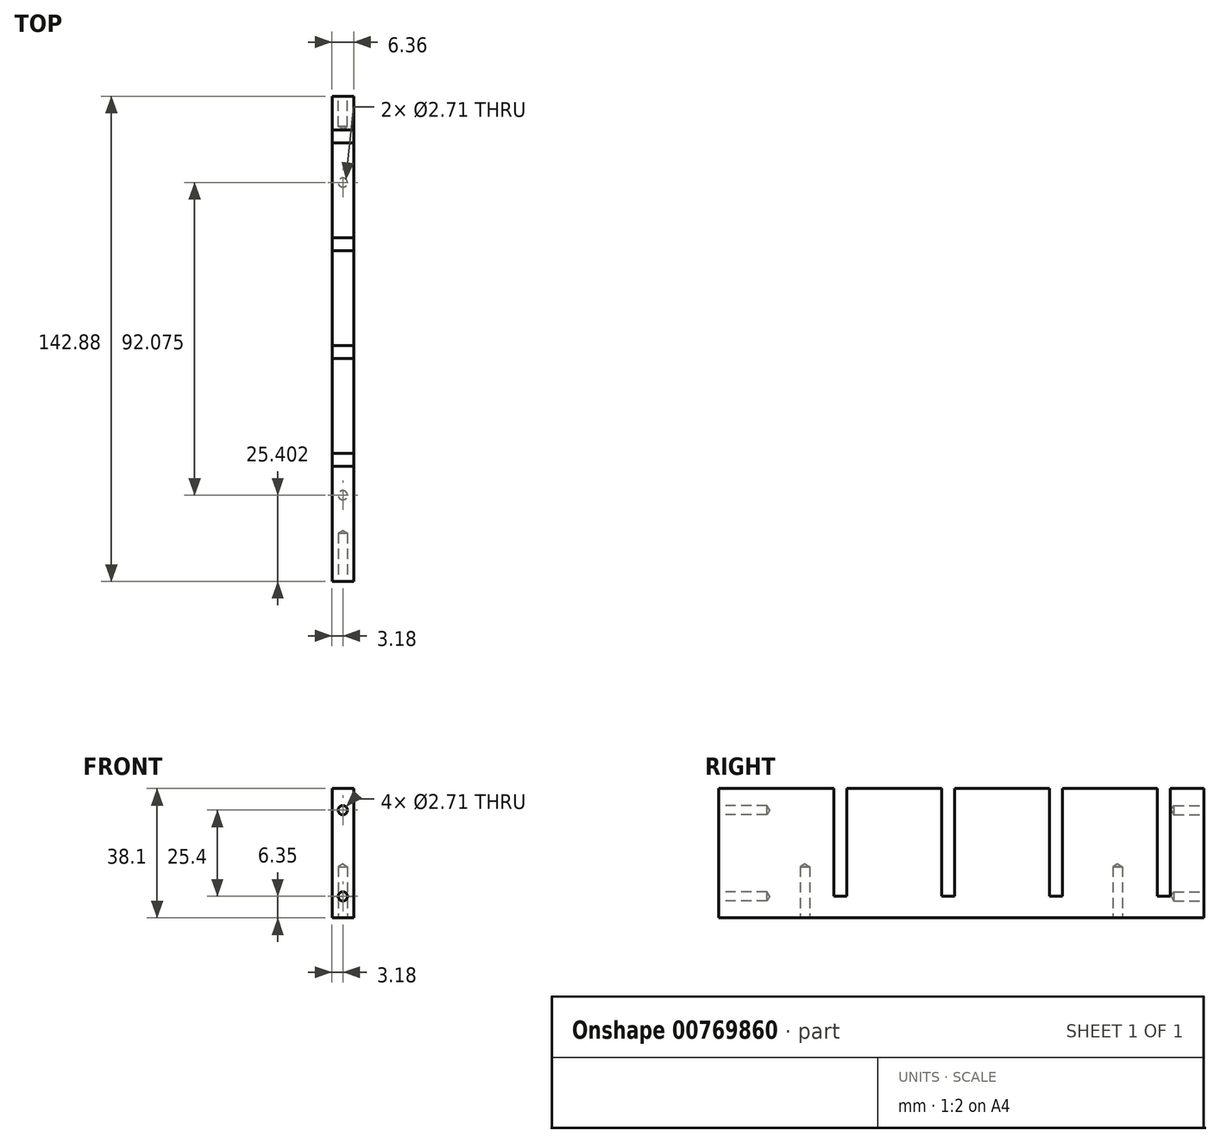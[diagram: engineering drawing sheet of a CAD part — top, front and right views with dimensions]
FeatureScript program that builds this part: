
annotation { "Feature Type Name" : "Feature", "Feature Type Description" : "" }
export const myFeature = defineFeature(function(context is Context, id is Id, definition is map)
    precondition{}
    {
        {
            var Q0;
            Q0=qCreatedBy(makeId("Top.planeOp"),FACE);
            var sketch = newSketch(context, id + "F0", { "sketchPlane" : qUnion([Q0])});
            skLineSegment(sketch, "E0.bottom", {"start": v(-3.17, 71.44) * mm, "end": v(3.18, 71.44) * mm});
            skLineSegment(sketch, "E0.top", {"start": v(-3.18, -71.44) * mm, "end": v(3.17, -71.44) * mm});
            skLineSegment(sketch, "E0.left", {"start": v(-3.17, 71.44) * mm, "end": v(-3.18, -71.44) * mm});
            skLineSegment(sketch, "E0.right", {"start": v(3.18, 71.44) * mm, "end": v(3.17, -71.44) * mm});
            skLineSegment(sketch, "E1", {"start": v(3.18, 71.44) * mm, "end": v(-3.18, -71.44) * mm, "construction": true});
            skSolve(sketch);
        }
        {
            var Q0;
            Q0=qSketchRegion(id+"F0",true);
            extrude(context, id + "F1", {"entities" : qUnion([Q0]), "depth" : 38.1 * mm, "offsetDistance" : 25.4 * mm});
        }
        {
            var Q0;
            Q0=makeQuery(id+"F1.opExtrude","SWEPT_FACE",FACE,{"disambiguationData":[OSD([sQuery(id+"F0.wireOp",EDGE,"E0.right")])]});
            var sketch = newSketch(context, id + "F2", { "sketchPlane" : qUnion([Q0])});
            skLineSegment(sketch, "E2", {"start": v(-71.44, 6.35) * mm, "end": v(71.44, 6.35) * mm, "construction": true});
            skLineSegment(sketch, "E3.bottom", {"start": v(61.53, 38.1) * mm, "end": v(57.72, 38.1) * mm});
            skLineSegment(sketch, "E3.top", {"start": v(61.53, 6.35) * mm, "end": v(57.72, 6.35) * mm});
            skLineSegment(sketch, "E3.left", {"start": v(61.53, 38.1) * mm, "end": v(61.53, 6.35) * mm});
            skLineSegment(sketch, "E3.right", {"start": v(57.72, 38.1) * mm, "end": v(57.72, 6.35) * mm});
            skLineSegment(sketch, "E4.bottom", {"start": v(29.78, 38.1) * mm, "end": v(25.97, 38.1) * mm});
            skLineSegment(sketch, "E4.top", {"start": v(29.78, 6.35) * mm, "end": v(25.97, 6.35) * mm});
            skLineSegment(sketch, "E4.left", {"start": v(29.78, 38.1) * mm, "end": v(29.78, 6.35) * mm});
            skLineSegment(sketch, "E4.right", {"start": v(25.97, 38.1) * mm, "end": v(25.97, 6.35) * mm});
            skLineSegment(sketch, "E5.bottom", {"start": v(-1.97, 38.1) * mm, "end": v(-5.78, 38.1) * mm});
            skLineSegment(sketch, "E5.top", {"start": v(-1.97, 6.35) * mm, "end": v(-5.78, 6.35) * mm});
            skLineSegment(sketch, "E5.left", {"start": v(-1.97, 38.1) * mm, "end": v(-1.97, 6.35) * mm});
            skLineSegment(sketch, "E5.right", {"start": v(-5.78, 38.1) * mm, "end": v(-5.78, 6.35) * mm});
            skLineSegment(sketch, "E6.bottom", {"start": v(-33.72, 38.1) * mm, "end": v(-37.53, 38.1) * mm});
            skLineSegment(sketch, "E6.top", {"start": v(-33.72, 6.35) * mm, "end": v(-37.53, 6.35) * mm});
            skLineSegment(sketch, "E6.left", {"start": v(-33.72, 38.1) * mm, "end": v(-33.72, 6.35) * mm});
            skLineSegment(sketch, "E6.right", {"start": v(-37.53, 38.1) * mm, "end": v(-37.53, 6.35) * mm});
            skPoint(sketch, "E7", {"position": v(59.62, 6.35) * mm});
            skPoint(sketch, "E8", {"position": v(27.87, 6.35) * mm});
            skPoint(sketch, "E9", {"position": v(-3.88, 6.35) * mm});
            skPoint(sketch, "E10", {"position": v(-35.63, 6.35) * mm});
            skSolve(sketch);
        }
        {
            var Q0;
            Q0 = qSketchRegion(id + "F2", true);
            extrude(context, id + "F3", {"entities" : qUnion([Q0]), "operationType" : NewBodyOperationType.REMOVE, "endBound" : BoundingType.THROUGH_ALL, "oppositeDirection" : true, "depth" : 25.4 * mm, "offsetDistance" : 25.4 * mm});
        }
        {
            var Q0;
            Q0=makeQuery(id+"F1.opExtrude","CAP_FACE",FACE,{"disambiguationData":[OSD([sQuery(id+"F0.wireOp",EDGE,"E0.bottom"),sQuery(id+"F0.wireOp",EDGE,"E0.top"),sQuery(id+"F0.wireOp",EDGE,"E0.left"),sQuery(id+"F0.wireOp",EDGE,"E0.right")])],"isStart":true});
            var sketch = newSketch(context, id + "F4", { "sketchPlane" : qUnion([Q0])});
            skLineSegment(sketch, "E11", {"start": v(0, 71.44) * mm, "end": v(0, -71.44) * mm, "construction": true});
            skPoint(sketch, "E12", {"position": v(0, 46.04) * mm});
            skPoint(sketch, "E13", {"position": v(0, -46.04) * mm});
            skSolve(sketch);
        }
        {
            var Q0;
            Q0=sQuery(id+"F4.wireOp",VERTEX,"E12");
            var Q1;
            Q1=sQuery(id+"F4.wireOp",VERTEX,"E13");
            var Q2;
            Q2=makeQuery(id+"F1.opExtrude","SWEPT_BODY",BODY,{"disambiguationData":[OSD([sQuery(id+"F0.wireOp",EDGE,"E0.bottom"),sQuery(id+"F0.wireOp",EDGE,"E0.top"),sQuery(id+"F0.wireOp",EDGE,"E0.left"),sQuery(id+"F0.wireOp",EDGE,"E0.right")])]});
            hole(context, id + "F5", {"style" : HoleStyle.SIMPLE, "endStyle" : HoleEndStyle.BLIND, "standardTappedOrClearance" : lookupTablePath({ "standard" : "ANSI", "engagement" : "75%", "pitch" : "32 tpi", "size" : "#6", "type" : "Tapped" }), "standardBlindInLast" : lookupTablePath({ "standard" : "ANSI", "engagement" : "75%", "pitch" : "32 tpi", "size" : "#6", "type" : "Tapped" }), "holeDiameter" : 2.7 * mm, "majorDiameter" : 3.5 * mm, "showTappedDepth" : true, "holeDepth" : 15.1 * mm, "tappedDepth" : 12.7 * mm, "tapClearance" : 3, "locations" : qUnion([Q0, Q1]), "scope" : qUnion([Q2])});
        }
        {
            var Q0;
            Q0=makeQuery(id+"F1.opExtrude","SWEPT_FACE",FACE,{"disambiguationData":[OSD([sQuery(id+"F0.wireOp",EDGE,"E0.bottom")])]});
            var sketch = newSketch(context, id + "F6", { "sketchPlane" : qUnion([Q0])});
            skLineSegment(sketch, "E14", {"start": v(0, 38.1) * mm, "end": v(0, 0) * mm, "construction": true});
            skPoint(sketch, "E15", {"position": v(0, 6.35) * mm});
            skPoint(sketch, "E16", {"position": v(0, 19.05) * mm});
            skPoint(sketch, "E17", {"position": v(0, 31.75) * mm});
            skSolve(sketch);
        }
        {
            var Q0;
            Q0=makeQuery(id+"F1.opExtrude","SWEPT_FACE",FACE,{"disambiguationData":[OSD([sQuery(id+"F0.wireOp",EDGE,"E0.top")])]});
            var sketch = newSketch(context, id + "F7", { "sketchPlane" : qUnion([Q0])});
            skLineSegment(sketch, "E18", {"start": v(0, 38.1) * mm, "end": v(0, 0) * mm, "construction": true});
            skPoint(sketch, "E19", {"position": v(0, 31.75) * mm});
            skPoint(sketch, "E20", {"position": v(0, 19.05) * mm});
            skPoint(sketch, "E21", {"position": v(0, 6.35) * mm});
            skSolve(sketch);
        }
        {
            var Q0;
            Q0=sQuery(id+"F7.wireOp",VERTEX,"E19");
            var Q1;
            Q1=sQuery(id+"F7.wireOp",VERTEX,"E21");
            var Q2;
            Q2=makeQuery(id+"F1.opExtrude","SWEPT_BODY",BODY,{"disambiguationData":[OSD([sQuery(id+"F0.wireOp",EDGE,"E0.bottom"),sQuery(id+"F0.wireOp",EDGE,"E0.top"),sQuery(id+"F0.wireOp",EDGE,"E0.left"),sQuery(id+"F0.wireOp",EDGE,"E0.right")])]});
            hole(context, id + "F8", {"style" : HoleStyle.SIMPLE, "endStyle" : HoleEndStyle.BLIND, "standardTappedOrClearance" : lookupTablePath({ "standard" : "ANSI", "engagement" : "75%", "pitch" : "32 tpi", "size" : "#6", "type" : "Tapped" }), "standardBlindInLast" : lookupTablePath({ "standard" : "ANSI", "engagement" : "75%", "pitch" : "32 tpi", "size" : "#6", "type" : "Tapped" }), "holeDiameter" : 2.7 * mm, "majorDiameter" : 3.5 * mm, "showTappedDepth" : true, "holeDepth" : 14.22 * mm, "tappedDepth" : 11.84 * mm, "tapClearance" : 3, "locations" : qUnion([Q0, Q1]), "scope" : qUnion([Q2])});
        }
        {
            var Q0;
            Q0=sQuery(id+"F6.wireOp",VERTEX,"E17");
            var Q1;
            Q1=sQuery(id+"F6.wireOp",VERTEX,"E15");
            var Q2;
            Q2=makeQuery(id+"F1.opExtrude","SWEPT_BODY",BODY,{"disambiguationData":[OSD([sQuery(id+"F0.wireOp",EDGE,"E0.bottom"),sQuery(id+"F0.wireOp",EDGE,"E0.top"),sQuery(id+"F0.wireOp",EDGE,"E0.left"),sQuery(id+"F0.wireOp",EDGE,"E0.right")])]});
            hole(context, id + "F9", {"style" : HoleStyle.SIMPLE, "endStyle" : HoleEndStyle.BLIND, "standardTappedOrClearance" : lookupTablePath({ "standard" : "ANSI", "engagement" : "75%", "pitch" : "32 tpi", "size" : "#6", "type" : "Tapped" }), "standardBlindInLast" : lookupTablePath({ "fit" : "Free", "standard" : "ANSI", "engagement" : "75%", "pitch" : "32 tpi", "size" : "#6", "type" : "Clearance & tapped" }), "holeDiameter" : 2.7 * mm, "majorDiameter" : 3.5 * mm, "showTappedDepth" : true, "holeDepth" : 8.9 * mm, "tappedDepth" : 6.5 * mm, "tapClearance" : 3, "locations" : qUnion([Q0, Q1]), "scope" : qUnion([Q2])});
        }
    });
